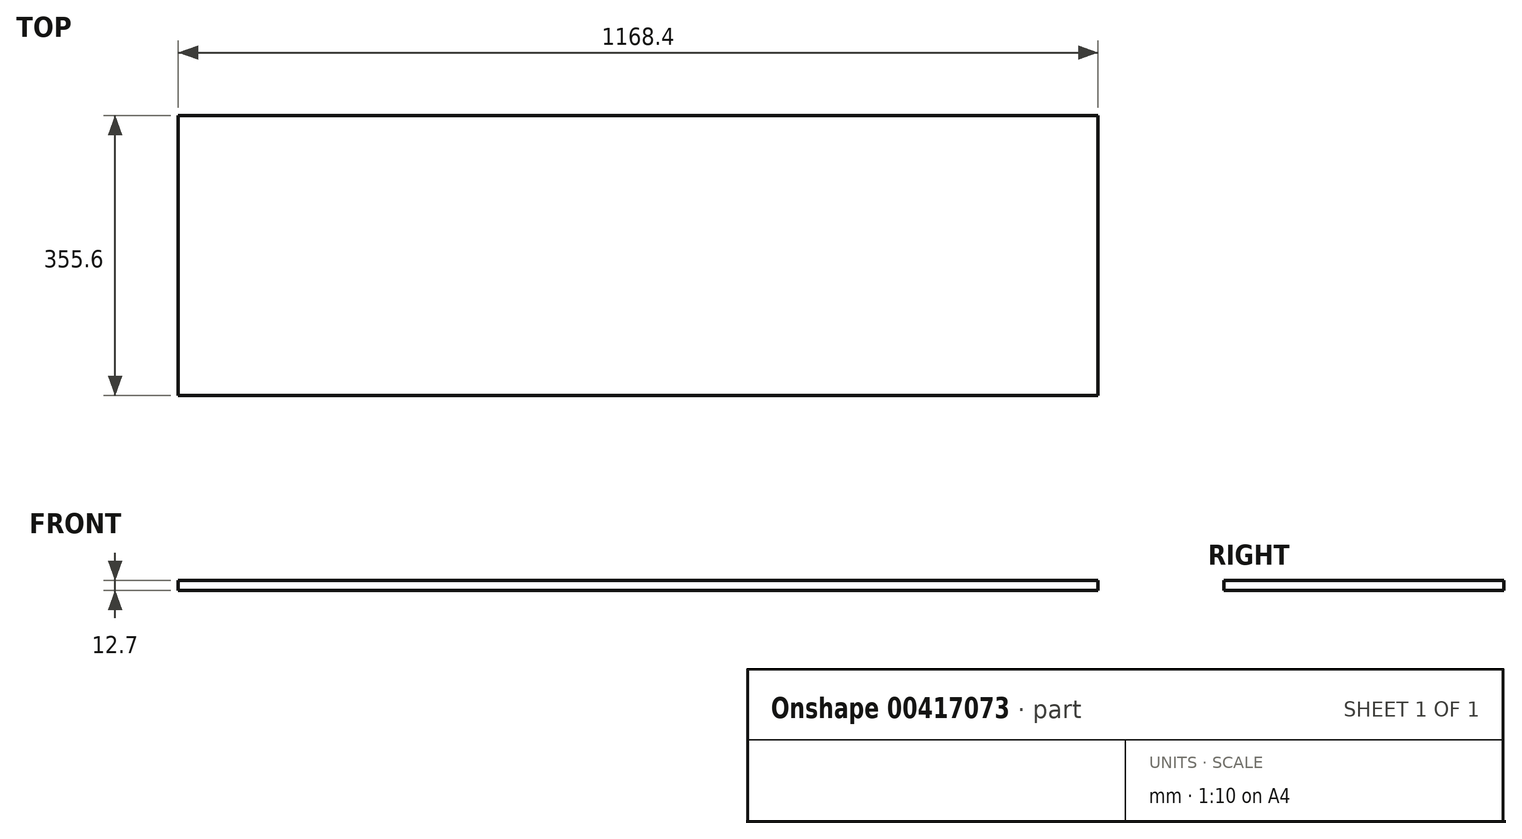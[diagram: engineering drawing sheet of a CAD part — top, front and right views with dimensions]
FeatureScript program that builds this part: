
annotation { "Feature Type Name" : "Feature", "Feature Type Description" : "" }
export const myFeature = defineFeature(function(context is Context, id is Id, definition is map)
    precondition{}
    {
        {
            var Q0;
            Q0=qCreatedBy(makeId("Top.planeOp"),FACE);
            var sketch = newSketch(context, id + "F0", { "sketchPlane" : qUnion([Q0])});
            skLineSegment(sketch, "E0.bottom", {"start": v(-584.2, 0) * mm, "end": v(584.2, 0) * mm});
            skLineSegment(sketch, "E0.top", {"start": v(-584.2, -355.6) * mm, "end": v(584.2, -355.6) * mm});
            skLineSegment(sketch, "E0.left", {"start": v(-584.2, 0) * mm, "end": v(-584.2, -355.6) * mm});
            skLineSegment(sketch, "E0.right", {"start": v(584.2, 0) * mm, "end": v(584.2, -355.6) * mm});
            skLineSegment(sketch, "E1", {"start": v(0, 0) * mm, "end": v(0, -355.6) * mm, "construction": true});
            skSolve(sketch);
        }
        {
            var Q0;
            Q0 = qSketchRegion(id + "F0", true);
            extrude(context, id + "F1", {"entities" : qUnion([Q0]), "depth" : 12.7 * mm});
        }
    });
